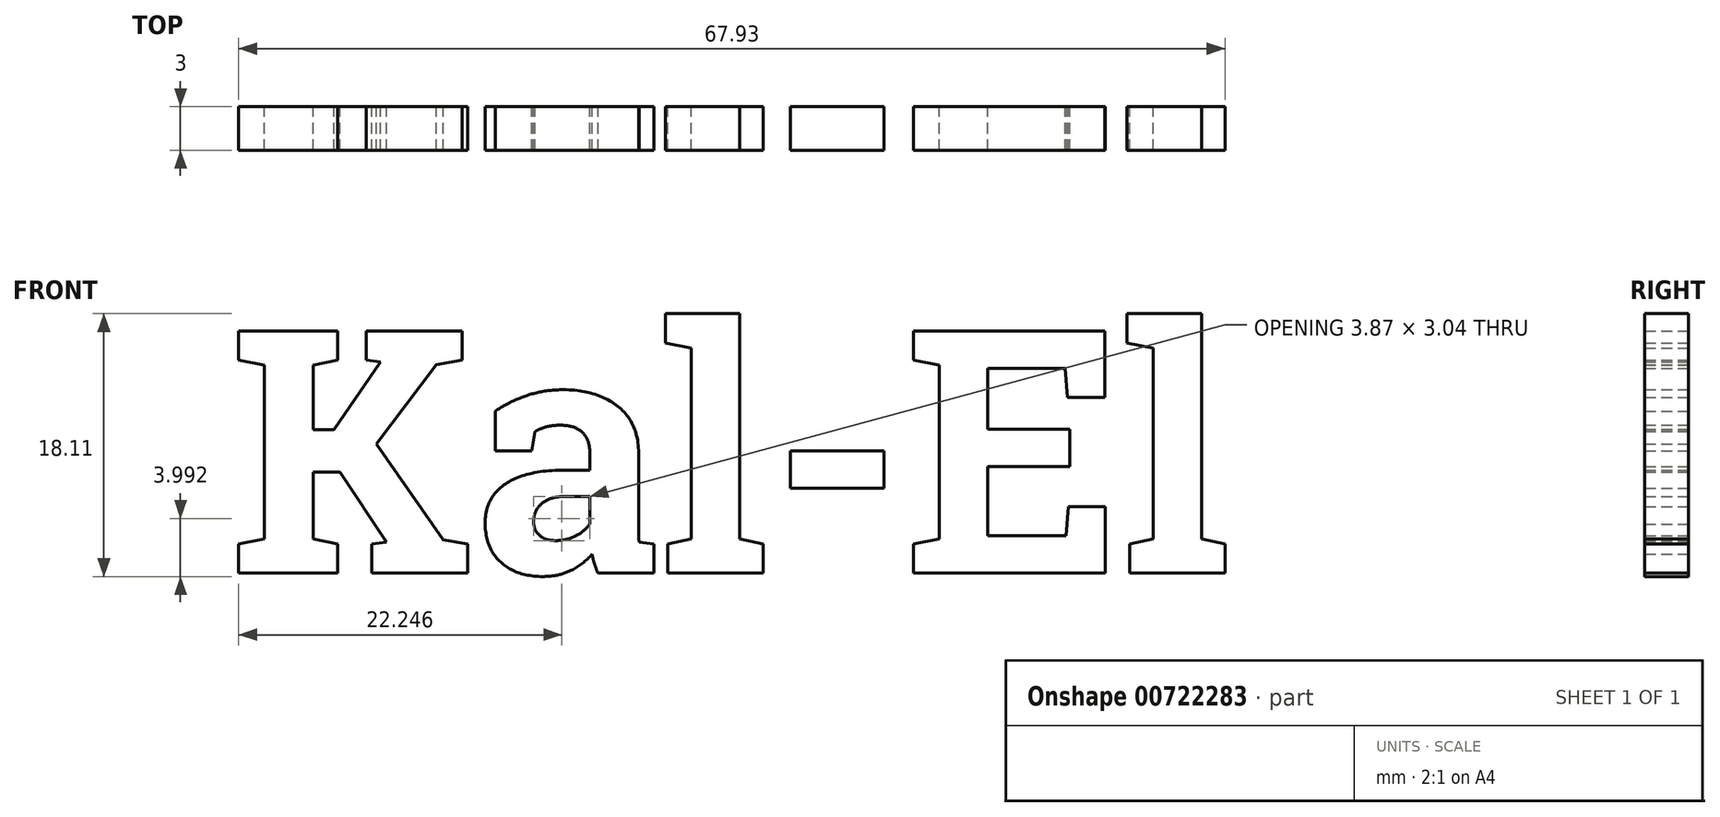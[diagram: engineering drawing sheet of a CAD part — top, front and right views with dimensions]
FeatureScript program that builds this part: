
annotation { "Feature Type Name" : "Feature", "Feature Type Description" : "" }
export const myFeature = defineFeature(function(context is Context, id is Id, definition is map)
    precondition{}
    {
        {
            var Q0;
            Q0=qCreatedBy(makeId("Front.planeOp"),FACE);
            var sketch = newSketch(context, id + "F0", { "sketchPlane" : qUnion([Q0])});
            skText(sketch, "E0", { "text": "Kal-El", "fontName": "RobotoSlab-Bold.ttf"});
            const initialGuessF0  = {"E0": [-0.02161, 0.0019, 1, 0, 0.01689]};
            skSetInitialGuess(sketch, initialGuessF0);
            skSolve(sketch);
        }
        {
            var Q0;
            Q0 = qSketchRegion(id + "F0", true);
            extrude(context, id + "F1", {"entities" : qUnion([Q0]), "depth" : 3 * mm, "offsetDistance" : 25 * mm});
        }
    });
